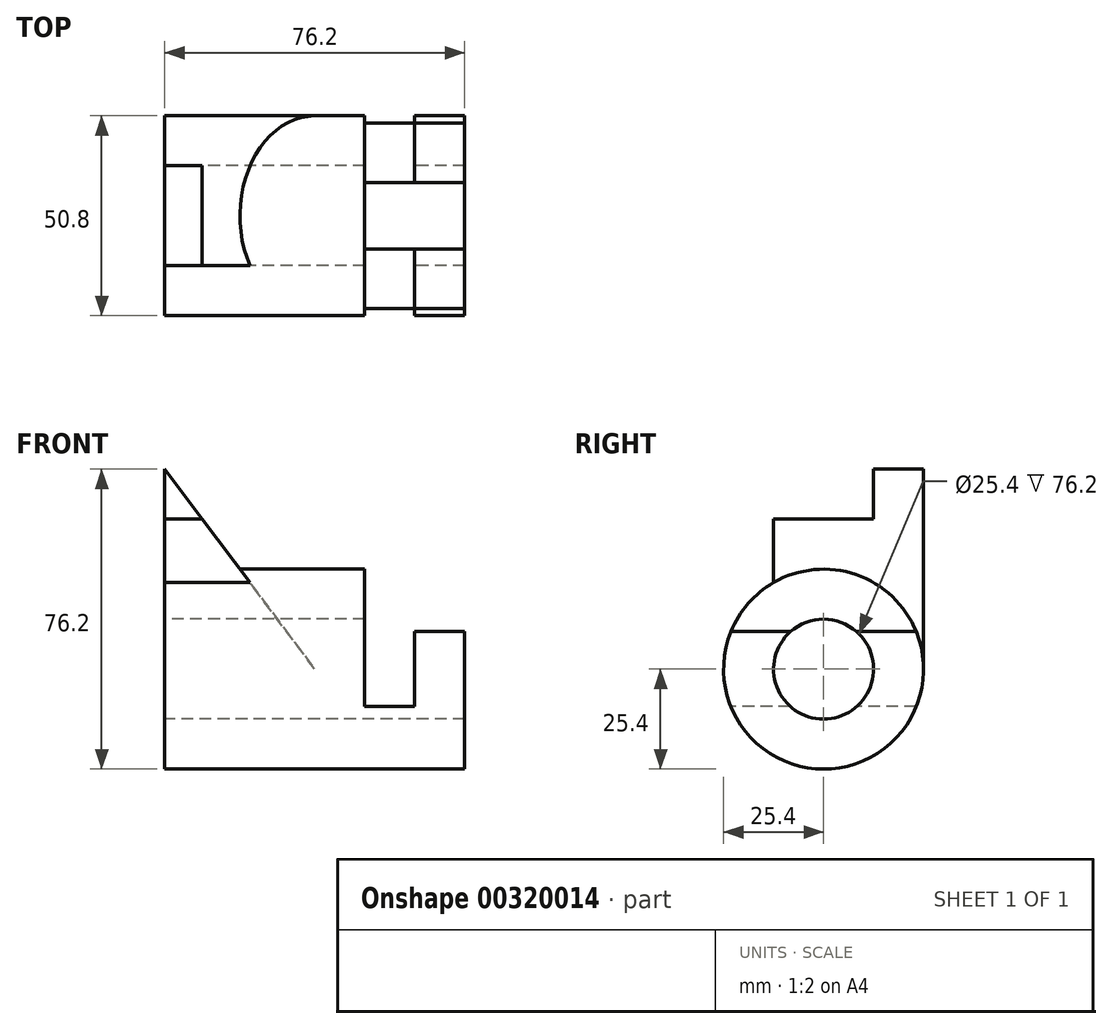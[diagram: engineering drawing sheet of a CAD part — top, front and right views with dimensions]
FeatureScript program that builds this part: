
annotation { "Feature Type Name" : "Feature", "Feature Type Description" : "" }
export const myFeature = defineFeature(function(context is Context, id is Id, definition is map)
    precondition{}
    {
        {
            var Q0;
            Q0=qCreatedBy(makeId("Right.planeOp"),FACE);
            var sketch = newSketch(context, id + "F0", { "sketchPlane" : qUnion([Q0])});
            skLineSegment(sketch, "E0", {"start": v(0, 0) * mm, "end": v(-12.7, 0) * mm});
            skLineSegment(sketch, "E1", {"start": v(-12.7, 0) * mm, "end": v(-12.7, 38.1) * mm});
            skLineSegment(sketch, "E2", {"start": v(-12.7, 38.1) * mm, "end": v(0, 38.1) * mm});
            skLineSegment(sketch, "E3", {"start": v(0, 38.1) * mm, "end": v(12.7, 38.1) * mm});
            skLineSegment(sketch, "E4", {"start": v(12.7, 38.1) * mm, "end": v(12.7, 50.8) * mm});
            skLineSegment(sketch, "E5", {"start": v(12.7, 50.8) * mm, "end": v(25.4, 50.8) * mm});
            skLineSegment(sketch, "E6", {"start": v(25.4, 50.8) * mm, "end": v(25.4, 0) * mm});
            skLineSegment(sketch, "E7", {"start": v(25.4, 0) * mm, "end": v(0, 0) * mm});
            skSolve(sketch);
        }
        {
            var Q0;
            Q0 = qSketchRegion(id + "F0", true);
            extrude(context, id + "F1", {"entities" : qUnion([Q0]), "depth" : 38.1 * mm});
        }
        {
            var Q0;
            Q0=qCreatedBy(makeId("Right.planeOp"),FACE);
            var sketch = newSketch(context, id + "F2", { "sketchPlane" : qUnion([Q0])});
            skCircle(sketch, "E8", {"center": v(0, 0) * mm, "radius": 25.4 * mm});
            skCircle(sketch, "E9", {"center": v(0, 0) * mm, "radius": 12.7 * mm});
            skSolve(sketch);
        }
        {
            var Q0;
            Q0=makeQuery(id+"F1.opExtrude","SWEPT_FACE",FACE,{"disambiguationData":[OSD([sQuery(id+"F0.wireOp",EDGE,"E6")])]});
            var sketch = newSketch(context, id + "F3", { "sketchPlane" : qUnion([Q0])});
            skLineSegment(sketch, "E10", {"start": v(-38.1, 0) * mm, "end": v(0, 50.8) * mm});
            skLineSegment(sketch, "E11", {"start": v(0, 50.8) * mm, "end": v(-38.1, 50.8) * mm});
            skLineSegment(sketch, "E12", {"start": v(-38.1, 50.8) * mm, "end": v(-38.1, 0) * mm});
            skSolve(sketch);
        }
        {
            var Q0;
            Q0 = qSketchRegion(id + "F3", true);
            extrude(context, id + "F4", {"entities" : qUnion([Q0]), "operationType" : NewBodyOperationType.REMOVE, "oppositeDirection" : true, "depth" : 38.1 * mm});
        }
        {
            var Q0;
            Q0 = qSketchRegion(id + "F2", true);
            extrude(context, id + "F5", {"entities" : qUnion([Q0]), "operationType" : NewBodyOperationType.ADD, "depth" : 76.2 * mm});
        }
        {
            var Q0;
            Q0=makeQuery(id+"F5.opExtrude","CAP_FACE",FACE,{"disambiguationData":[OSD([sQuery(id+"F2.wireOp",EDGE,"E8"),sQuery(id+"F2.wireOp",EDGE,"E9")])],"isStart":false});
            var sketch = newSketch(context, id + "F6", { "sketchPlane" : qUnion([Q0])});
            skLineSegment(sketch, "E13", {"start": v(0, 25.4) * mm, "end": v(0, 9.53) * mm});
            skLineSegment(sketch, "E14", {"start": v(0, 9.53) * mm, "end": v(23.55, 9.53) * mm});
            skLineSegment(sketch, "E15", {"start": v(23.55, 9.53) * mm, "end": v(-23.55, 9.53) * mm});
            skLineSegment(sketch, "E16", {"start": v(-23.55, 9.53) * mm, "end": v(-23.55, 25.4) * mm});
            skLineSegment(sketch, "E17", {"start": v(-23.55, 25.4) * mm, "end": v(23.55, 25.4) * mm});
            skLineSegment(sketch, "E18", {"start": v(23.55, 25.4) * mm, "end": v(23.55, 9.53) * mm});
            skSolve(sketch);
        }
        {
            var Q0;
            Q0 = qSketchRegion(id + "F6", true);
            extrude(context, id + "F7", {"entities" : qUnion([Q0]), "operationType" : NewBodyOperationType.REMOVE, "oppositeDirection" : true, "depth" : 25.4 * mm});
        }
        {
            var Q0;
            Q0=makeQuery(id+"F7.boolean.opBoolean","COPY",FACE,{"disambiguationData":[OD(0.0)],"derivedFrom":makeQuery(id+"F7.opExtrude","SWEPT_FACE",FACE,{"disambiguationData":[OSD([sQuery(id+"F6.wireOp",EDGE,"E15")])]})});
            var sketch = newSketch(context, id + "F8", { "sketchPlane" : qUnion([Q0])});
            skLineSegment(sketch, "E19", {"start": v(63.5, 8.4) * mm, "end": v(63.5, 27.77) * mm});
            skPoint(sketch, "E19.endSnap0", {"position": v(63.5, 23.55) * mm});
            skLineSegment(sketch, "E20", {"start": v(63.5, 27.77) * mm, "end": v(50.8, 27.77) * mm});
            skLineSegment(sketch, "E21", {"start": v(50.8, 27.77) * mm, "end": v(50.8, -27.77) * mm});
            skLineSegment(sketch, "E22", {"start": v(50.8, -27.77) * mm, "end": v(63.5, -27.77) * mm});
            skLineSegment(sketch, "E23", {"start": v(63.5, -27.77) * mm, "end": v(63.5, 8.4) * mm});
            skSolve(sketch);
        }
        {
            var Q0;
            Q0 = qSketchRegion(id + "F8", true);
            extrude(context, id + "F9", {"entities" : qUnion([Q0]), "operationType" : NewBodyOperationType.REMOVE, "oppositeDirection" : true, "depth" : 19.05 * mm});
        }
        {
            var Q0;
            Q0=makeQuery(id+"F2.imprint","IMPRINT",FACE,{"disambiguationData":[TD([[makeQuery(id+"F2.imprint","IMPRINT",EDGE,{"derivedFrom":sQuery(id+"F2.wireOp",EDGE,"E9")}),1.0]])]});
            extrude(context, id + "F10", {"entities" : qUnion([Q0]), "operationType" : NewBodyOperationType.REMOVE, "endBound" : BoundingType.THROUGH_ALL, "oppositeDirection" : true, "depth" : 25.4 * mm});
        }
        {
            var Q0;
            Q0=makeQuery(id+"F5.boolean.opBoolean","MERGE",FACE,{"derivedFrom":[makeQuery(id+"F1.opExtrude","CAP_FACE",FACE,{"disambiguationData":[OSD([sQuery(id+"F0.wireOp",EDGE,"E0"),sQuery(id+"F0.wireOp",EDGE,"E1"),sQuery(id+"F0.wireOp",EDGE,"E2"),sQuery(id+"F0.wireOp",EDGE,"E3"),sQuery(id+"F0.wireOp",EDGE,"E4"),sQuery(id+"F0.wireOp",EDGE,"E5"),sQuery(id+"F0.wireOp",EDGE,"E6"),sQuery(id+"F0.wireOp",EDGE,"E7")])],"isStart":true}),makeQuery(id+"F5.opExtrude","CAP_FACE",FACE,{"disambiguationData":[OSD([sQuery(id+"F2.wireOp",EDGE,"E8"),sQuery(id+"F2.wireOp",EDGE,"E9")])],"isStart":true})]});
            var sketch = newSketch(context, id + "F11", { "sketchPlane" : qUnion([Q0])});
            skCircle(sketch, "E24", {"center": v(0, 0) * mm, "radius": 12.7 * mm});
            skSolve(sketch);
        }
        {
            var Q0;
            Q0 = qSketchRegion(id + "F11", true);
            extrude(context, id + "F12", {"entities" : qUnion([Q0]), "operationType" : NewBodyOperationType.REMOVE, "endBound" : BoundingType.THROUGH_ALL, "oppositeDirection" : true, "depth" : 25.4 * mm});
        }
    });
